# Revit family: HVAC_Heat-Pumps_HAJDU_HAJDU-HPAW-4-6_1
name_source: partatom
category: Mechanical Equipment
units: mm (PartAtom-declared; Revit-internal decimal feet)

## family parameters
Always vertical = Yes
Classification = None
Cut with Voids When Loaded = No
Maintain Annotation Orientation = No
OmniClass Number = 23.33.17.00
OmniClass Title = Heat Pumps
Part Type = Normal
Room Calculation Point = No
Round Connector Dimension = Use Diameter
Shared = No
Work Plane-Based = Yes

## types (2) — shared parameters
Default Elevation = 1219.2 mm  [stored 4 ft]
Description = A HPAW levegő vizes hőszivattyú komplett megoldást nyújthat fűtésre, hűtésre, használati melegvíz előállításra, széles környezeti tartományban. Ideális megoldás meglévő és új építésű ingatlanok korszerű és környezetkímélő fűtési és klimatizációs rendszerének kiépítéséhez, vagy korszerűsítéséhez. Kiegészíthető akár hagyományos, gáz, vagy más fűtési rendszerekkel is. Monoblokk kialakítású, a hőszivattyú és a hydrobox egy készülékházban helyezkedik el. Ezek a készülékek egy fázisúak. Méretükben eltérnek a 8kW vagy nagyobb teljesítményűektől. A hydrobox és a hőszivattyú egyetlen nagy ajtó mögött található kompakt módon. Elektromos fűtőpatron nélküli verziójuk is kapható, ám az üzembiztonságot szem előtt tartva, többségében már ezekkel kiegészülve érkeznek.
Előremenő hőmérséklet tartomány, Fütés = 25～65 °C
Előremenő hőmérséklet tartomány, Hutés = 5～25 °C
Előremenő hőmérséklet tartomány, Melegvíz = 30～60 °C
Feszültség = 230 V
Frekvencia = 50 Hz
Futés 1 Felvett teljesítmény = 1 kW
Futés 3 COP = 2.95
Fázisok száma = 1
Hutoközeg Töltotömeg = 1.4 kg
Hutés 4 Felvett teljesítmény = 1 kW
Házház anyaga = Hajdu - Felület - Fehér
Hűtőközeg Típus (GWP) = R32(675)
Kiegészíto elektromos futés, Sztenderd szerelés = 3 kW
Kiegészíto elektromos futés, Áramellátás = 220-240/1/50
Kulso levego homérséklet, Hutés = -5～43 °C
Külso levego homérséklet, Fütés = -25～35 °C
Külso levego homérséklet, Melegvíz = -25～43 °C
Magasság = 718 mm  [stored 2.35564 ft]
Manufacturer = HAJDU
Mélység = 429 mm  [stored 1.40748 ft]
Product Page URL = https://hajdurt.hu
Szezonális helyiség futési energiahatékonysági osztály, Elóremenó  55 °C-on = A++
Szezonális helyiség futési energiahatékonysági osztály, Elóremenó 35 °C = A+++
Szivattyú Emelo magasság = 9 m
Szélesség = 1295 mm
Teljesítménytényezo = 1
Tömeg = 98.00 kg
URL = https://hajdurt.hu
Vízcsatlakozás = 25.4 mm  [stored 0.0833333 ft]
Vízoldali hocserélo = Lemezes típus
szabad tér hozzáférés bal oldalon = 500 mm  [stored 1.64042 ft]
szabad tér hozzáférés elöl = 1000 mm  [stored 3.28084 ft]
szabad tér hozzáférés felül = 200 mm  [stored 0.656168 ft]
szabad tér hozzáférés hátul = 300 mm
szabad tér hozzáférés jobb oldalon = 500 mm  [stored 1.64042 ft]

## per-type parameters (varying)
| type | Futés 1 COP | Futés 1 Teljesítmény | Futés 2 COP | Futés 2 Felvett teljesítmény | Futés 2 Teljesítmény | Futés 3 Felvett teljesítmény | Futés 3 Teljesítmény | Hutés 4 EER | Hutés 4 Teljesítmény | Hutés 5 EER | Hutés 5 Felvett teljesítmény | Hutés 5 Teljesítmény | Látszólagos terhelés | Zajszint | Áramfelvétel |
| HPAW 4kW | 5.10 | 4 kW | 3.80 | 1 kW | 4 kW | 1 kW | 4 kW | 5.50 | 5 kW | 3.45 | 1 kW | 5 kW | 2645 VA | 55 dB | 12 A |
| HPAW 6kW | 4.95 | 6 kW | 3.70 | 2 kW | 6 kW | 2 kW | 6 kW | 4.80 | 7 kW | 3.00 | 2 kW | 7 kW | 3105 VA | 58 dB | 14 A |

note: column(s) folded — value = type name in every type: Model

note: [stored X ft] marks values corroborated as IEEE doubles in the binary element streams (Revit-internal decimal feet)

## geometry (parser evidence)
native form markers: Sweep x4
no freeform markers — native parametric forms only
